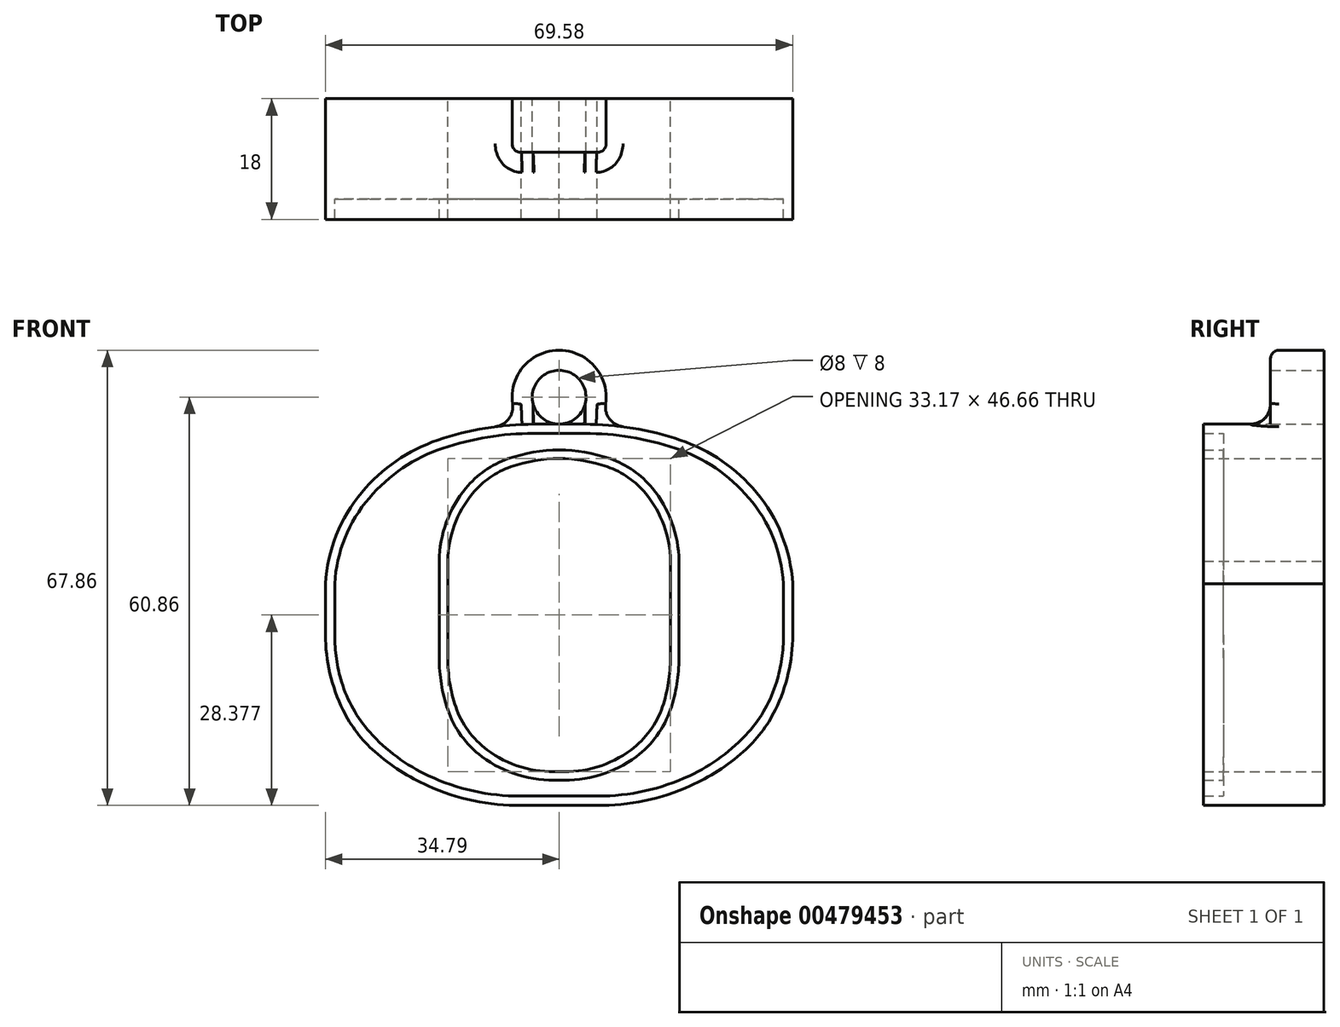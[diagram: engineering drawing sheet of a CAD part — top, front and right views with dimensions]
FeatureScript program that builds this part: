
annotation { "Feature Type Name" : "Feature", "Feature Type Description" : "" }
export const myFeature = defineFeature(function(context is Context, id is Id, definition is map)
    precondition{}
    {
        {
            var Q0;
            Q0=qCreatedBy(makeId("Front.planeOp"),FACE);
            var sketch = newSketch(context, id + "F0", { "sketchPlane" : qUnion([Q0])});
            skLineSegment(sketch, "E0", {"start": v(0, 23.85) * mm, "end": v(9.94, 23.85) * mm, "construction": true});
            skLineSegment(sketch, "E1", {"start": v(-16.59, 8.55) * mm, "end": v(-16.59, -5.87) * mm});
            skLineSegment(sketch, "E2", {"start": v(0, 23.85) * mm, "end": v(0, 28.97) * mm, "construction": true});
            skLineSegment(sketch, "E3", {"start": v(0, 28.97) * mm, "end": v(-3.73, 28.97) * mm});
            skArc(sketch, "E4", {"start": v(-3.73, 28.97) * mm, "mid": v(-11, 28.37) * mm, "end": v(-18.07, 26.6) * mm});
            skArc(sketch, "E5", {"start": v(-18.07, 26.6) * mm, "mid": v(-24.27, 23.48) * mm, "end": v(-29.4, 18.8) * mm});
            skArc(sketch, "E6", {"start": v(-29.4, 18.8) * mm, "mid": v(-33.17, 12.43) * mm, "end": v(-34.79, 5.2) * mm});
            skLineSegment(sketch, "E7", {"start": v(-34.79, 5.2) * mm, "end": v(-34.79, -2.41) * mm});
            skArc(sketch, "E8", {"start": v(-34.79, -2.41) * mm, "mid": v(-34.13, -8.18) * mm, "end": v(-32.18, -13.64) * mm});
            skArc(sketch, "E9", {"start": v(-32.18, -13.64) * mm, "mid": v(-30.11, -16.97) * mm, "end": v(-27.44, -19.84) * mm});
            skArc(sketch, "E10", {"start": v(-27.44, -19.84) * mm, "mid": v(-23.69, -22.68) * mm, "end": v(-19.55, -24.94) * mm});
            skArc(sketch, "E11", {"start": v(-19.55, -24.94) * mm, "mid": v(-12.76, -27.16) * mm, "end": v(-5.64, -27.86) * mm});
            skLineSegment(sketch, "E12", {"start": v(0, -22.8) * mm, "end": v(0, -27.86) * mm, "construction": true});
            skArc(sketch, "E13", {"start": v(0, 23.85) * mm, "mid": v(-3.64, 23.54) * mm, "end": v(-7.17, 22.63) * mm});
            skArc(sketch, "E14", {"start": v(-7.17, 22.63) * mm, "mid": v(-10.32, 21.01) * mm, "end": v(-12.9, 18.62) * mm});
            skArc(sketch, "E15", {"start": v(-12.9, 18.62) * mm, "mid": v(-15.6, 13.9) * mm, "end": v(-16.59, 8.55) * mm});
            skArc(sketch, "E16", {"start": v(-16.59, -5.87) * mm, "mid": v(-16.29, -9.56) * mm, "end": v(-15.4, -13.14) * mm});
            skArc(sketch, "E17", {"start": v(-15.4, -13.14) * mm, "mid": v(-13.55, -16.71) * mm, "end": v(-10.73, -19.57) * mm});
            skArc(sketch, "E18", {"start": v(-10.73, -19.57) * mm, "mid": v(-5.65, -22.13) * mm, "end": v(0, -22.8) * mm});
            skArc(sketch, "E19.0", {"start": v(-11.49, -20.59) * mm, "mid": v(-6.01, -23.35) * mm, "end": v(0.07, -24.06) * mm});
            skArc(sketch, "E19.1", {"start": v(-16.6, -13.55) * mm, "mid": v(-14.58, -17.46) * mm, "end": v(-11.49, -20.59) * mm});
            skArc(sketch, "E19.2", {"start": v(-17.86, -5.87) * mm, "mid": v(-17.54, -9.76) * mm, "end": v(-16.6, -13.55) * mm});
            skArc(sketch, "E19.3", {"start": v(0, 25.12) * mm, "mid": v(-3.85, 24.8) * mm, "end": v(-7.6, 23.82) * mm});
            skArc(sketch, "E19.4", {"start": v(-7.6, 23.82) * mm, "mid": v(-11.04, 22.06) * mm, "end": v(-13.89, 19.42) * mm});
            skArc(sketch, "E19.5", {"start": v(-13.89, 19.42) * mm, "mid": v(-16.8, 14.33) * mm, "end": v(-17.86, 8.56) * mm});
            skLineSegment(sketch, "E19.6", {"start": v(-17.86, 8.56) * mm, "end": v(-17.86, -5.87) * mm});
            skLineSegment(sketch, "E20", {"start": v(0, 27.6) * mm, "end": v(-3.8, 27.6) * mm});
            skArc(sketch, "E21", {"start": v(-3.8, 27.6) * mm, "mid": v(-10.65, 27.04) * mm, "end": v(-17.31, 25.39) * mm});
            skArc(sketch, "E22", {"start": v(-17.31, 25.39) * mm, "mid": v(-23.3, 22.43) * mm, "end": v(-28.27, 17.98) * mm});
            skArc(sketch, "E23", {"start": v(-28.27, 17.98) * mm, "mid": v(-31.9, 12) * mm, "end": v(-33.42, 5.2) * mm});
            skLineSegment(sketch, "E24", {"start": v(-33.42, 5.2) * mm, "end": v(-33.42, -2.42) * mm});
            skArc(sketch, "E25", {"start": v(-33.42, -2.42) * mm, "mid": v(-33.16, -6) * mm, "end": v(-32.38, -9.48) * mm});
            skArc(sketch, "E26", {"start": v(-32.38, -9.48) * mm, "mid": v(-30.7, -13.43) * mm, "end": v(-28.2, -16.93) * mm});
            skArc(sketch, "E27", {"start": v(-28.2, -16.93) * mm, "mid": v(-24.14, -20.63) * mm, "end": v(-19.43, -23.44) * mm});
            skArc(sketch, "E28", {"start": v(-19.43, -23.44) * mm, "mid": v(-12.77, -25.7) * mm, "end": v(-5.76, -26.45) * mm});
            skLineSegment(sketch, "E29", {"start": v(-5.76, -26.45) * mm, "end": v(0, -26.45) * mm});
            skArc(sketch, "E30.MirrorCS", {"start": v(34.79, -2.41) * mm, "mid": v(34.13, -8.18) * mm, "end": v(32.18, -13.64) * mm});
            skLineSegment(sketch, "E31.MirrorCS", {"start": v(34.79, 5.2) * mm, "end": v(34.79, -2.41) * mm});
            skArc(sketch, "E32.MirrorCS", {"start": v(29.4, 18.8) * mm, "mid": v(33.17, 12.43) * mm, "end": v(34.79, 5.2) * mm});
            skLineSegment(sketch, "E33.MirrorCS", {"start": v(0, 27.6) * mm, "end": v(3.8, 27.6) * mm});
            skLineSegment(sketch, "E34.MirrorCS", {"start": v(0, 28.97) * mm, "end": v(3.73, 28.97) * mm});
            skArc(sketch, "E35.MirrorCS", {"start": v(0, 25.12) * mm, "mid": v(3.85, 24.8) * mm, "end": v(7.6, 23.82) * mm});
            skArc(sketch, "E36.MirrorCS", {"start": v(0, 23.85) * mm, "mid": v(3.64, 23.54) * mm, "end": v(7.17, 22.63) * mm});
            skArc(sketch, "E37.MirrorCS", {"start": v(19.43, -23.44) * mm, "mid": v(12.77, -25.7) * mm, "end": v(5.76, -26.45) * mm});
            skLineSegment(sketch, "E38.MirrorCS", {"start": v(33.42, 5.2) * mm, "end": v(33.42, -2.42) * mm});
            skArc(sketch, "E39.MirrorCS", {"start": v(10.73, -19.57) * mm, "mid": v(5.65, -22.13) * mm, "end": v(0, -22.8) * mm});
            skArc(sketch, "E40.MirrorCS", {"start": v(12.9, 18.62) * mm, "mid": v(15.6, 13.9) * mm, "end": v(16.59, 8.55) * mm});
            skArc(sketch, "E41.MirrorCS", {"start": v(33.42, -2.42) * mm, "mid": v(33.16, -6) * mm, "end": v(32.38, -9.48) * mm});
            skArc(sketch, "E42.MirrorCS", {"start": v(13.89, 19.42) * mm, "mid": v(16.8, 14.33) * mm, "end": v(17.86, 8.56) * mm});
            skArc(sketch, "E43.MirrorCS", {"start": v(3.8, 27.6) * mm, "mid": v(10.65, 27.04) * mm, "end": v(17.31, 25.39) * mm});
            skArc(sketch, "E44.MirrorCS", {"start": v(27.44, -19.84) * mm, "mid": v(23.69, -22.68) * mm, "end": v(19.55, -24.94) * mm});
            skArc(sketch, "E45.MirrorCS", {"start": v(18.07, 26.6) * mm, "mid": v(24.27, 23.48) * mm, "end": v(29.4, 18.8) * mm});
            skArc(sketch, "E46.MirrorCS", {"start": v(28.2, -16.93) * mm, "mid": v(24.14, -20.63) * mm, "end": v(19.43, -23.44) * mm});
            skArc(sketch, "E47.MirrorCS", {"start": v(15.4, -13.14) * mm, "mid": v(13.55, -16.71) * mm, "end": v(10.73, -19.57) * mm});
            skArc(sketch, "E48.MirrorCS", {"start": v(11.49, -20.59) * mm, "mid": v(6.01, -23.35) * mm, "end": v(-0.07, -24.06) * mm});
            skArc(sketch, "E49.MirrorCS", {"start": v(28.27, 17.98) * mm, "mid": v(31.9, 12) * mm, "end": v(33.42, 5.2) * mm});
            skArc(sketch, "E50.MirrorCS", {"start": v(16.59, -5.87) * mm, "mid": v(16.29, -9.56) * mm, "end": v(15.4, -13.14) * mm});
            skArc(sketch, "E51.MirrorCS", {"start": v(7.6, 23.82) * mm, "mid": v(11.04, 22.06) * mm, "end": v(13.89, 19.42) * mm});
            skArc(sketch, "E52.MirrorCS", {"start": v(16.6, -13.55) * mm, "mid": v(14.58, -17.46) * mm, "end": v(11.49, -20.59) * mm});
            skArc(sketch, "E53.MirrorCS", {"start": v(3.73, 28.97) * mm, "mid": v(11, 28.37) * mm, "end": v(18.07, 26.6) * mm});
            skArc(sketch, "E54.MirrorCS", {"start": v(17.31, 25.39) * mm, "mid": v(23.3, 22.43) * mm, "end": v(28.27, 17.98) * mm});
            skArc(sketch, "E55.MirrorCS", {"start": v(7.17, 22.63) * mm, "mid": v(10.32, 21.01) * mm, "end": v(12.9, 18.62) * mm});
            skLineSegment(sketch, "E56.MirrorCS", {"start": v(16.59, 8.55) * mm, "end": v(16.59, -5.87) * mm});
            skArc(sketch, "E57.MirrorCS", {"start": v(32.18, -13.64) * mm, "mid": v(30.11, -16.97) * mm, "end": v(27.44, -19.84) * mm});
            skArc(sketch, "E58.MirrorCS", {"start": v(17.86, -5.87) * mm, "mid": v(17.54, -9.76) * mm, "end": v(16.6, -13.55) * mm});
            skLineSegment(sketch, "E59.MirrorCS", {"start": v(5.76, -26.45) * mm, "end": v(0, -26.45) * mm});
            skLineSegment(sketch, "E60.MirrorCS", {"start": v(17.86, 8.56) * mm, "end": v(17.86, -5.87) * mm});
            skArc(sketch, "E61.MirrorCS", {"start": v(19.55, -24.94) * mm, "mid": v(12.76, -27.16) * mm, "end": v(5.64, -27.86) * mm});
            skArc(sketch, "E62.MirrorCS", {"start": v(32.38, -9.48) * mm, "mid": v(30.7, -13.43) * mm, "end": v(28.2, -16.93) * mm});
            skLineSegment(sketch, "E63", {"start": v(-5.64, -27.86) * mm, "end": v(5.64, -27.86) * mm});
            skSolve(sketch);
        }
        {
            var Q0;
            Q0 = qSketchRegion(id + "F0", true);
            var Q1;
            Q1=makeQuery(id+"F0.imprint","IMPRINT",FACE,{"disambiguationData":[TD([[makeQuery(id+"F0.imprint","IMPRINT",EDGE,{"derivedFrom":sQuery(id+"F0.wireOp",EDGE,"E1")}),-1.0]])]});
            var Q2;
            {var subQ0=sQuery(id+"F0.wireOp",EDGE,"E19.1");Q2=makeQuery(id+"F0.imprint","IMPRINT",FACE,{"disambiguationData":[TD([[makeQuery(id+"F0.imprint","IMPRINT",EDGE,{"derivedFrom":subQ0}),-1.0]])]});}
            extrude(context, id + "F1", {"entities" : qUnion([Q0, Q1, Q2]), "depth" : 15 * mm});
        }
        {
            var Q0;
            Q0=makeQuery(id+"F0.imprint","IMPRINT",FACE,{"disambiguationData":[TD([[makeQuery(id+"F0.imprint","IMPRINT",EDGE,{"derivedFrom":sQuery(id+"F0.wireOp",EDGE,"E1")}),-1.0]])]});
            var Q1;
            Q1=makeQuery(id+"F0.imprint","IMPRINT",FACE,{"disambiguationData":[TD([[makeQuery(id+"F0.imprint","IMPRINT",EDGE,{"derivedFrom":sQuery(id+"F0.wireOp",EDGE,"E3")}),1.0]])]});
            extrude(context, id + "F2", {"entities" : qUnion([Q0, Q1]), "operationType" : NewBodyOperationType.ADD, "depth" : 18 * mm});
        }
        {
            var Q0;
            Q0=qCreatedBy(makeId("Front.planeOp"),FACE);
            var sketch = newSketch(context, id + "F3", { "sketchPlane" : qUnion([Q0])});
            skLineSegment(sketch, "E64", {"start": v(0, 0) * mm, "end": v(0, 26) * mm});
            skCircle(sketch, "E65", {"center": v(0, 33) * mm, "radius": 7 * mm});
            skCircle(sketch, "E66", {"center": v(0, 33) * mm, "radius": 4 * mm});
            skSolve(sketch);
        }
        {
            var Q0;
            Q0 = qSketchRegion(id + "F3", true);
            extrude(context, id + "F4", {"entities" : qUnion([Q0]), "operationType" : NewBodyOperationType.ADD, "depth" : 8 * mm});
        }
        {
            var Q0;
            Q0=makeQuery(id+"F4.opExtrude","CAP_EDGE",EDGE,{"disambiguationData":[OSD([sQuery(id+"F3.wireOp",EDGE,"E65")])],"isStart":false});
            fillet(context, id + "F5", {"entities" : qUnion([Q0]), "radius" : 1.25 * mm, "tangentPropagation" : true, "allowEdgeOverflow" : false});
        }
        {
            var Q0;
            {var subQ0=sQuery(id+"F0.wireOp",EDGE,"E53.MirrorCS");Q0=makeQuery(id+"F4.boolean.opBoolean","INTERSECT",EDGE,{"derivedFrom":[makeQuery(id+"F2.boolean.opBoolean","MERGE",FACE,{"derivedFrom":[makeQuery(id+"F1.opExtrude","SWEPT_FACE",FACE,{"disambiguationData":[OSD([subQ0])]}),makeQuery(id+"F2.opExtrude","SWEPT_FACE",FACE,{"disambiguationData":[OSD([subQ0])]})]}),makeQuery(id+"F4.opExtrude","SWEPT_FACE",FACE,{"disambiguationData":[OSD([sQuery(id+"F3.wireOp",EDGE,"E65")])]})]});}
            var Q1;
            {var subQ0=sQuery(id+"F0.wireOp",EDGE,"E4");Q1=makeQuery(id+"F4.boolean.opBoolean","INTERSECT",EDGE,{"derivedFrom":[makeQuery(id+"F2.boolean.opBoolean","MERGE",FACE,{"derivedFrom":[makeQuery(id+"F1.opExtrude","SWEPT_FACE",FACE,{"disambiguationData":[OSD([subQ0])]}),makeQuery(id+"F2.opExtrude","SWEPT_FACE",FACE,{"disambiguationData":[OSD([subQ0])]})]}),makeQuery(id+"F4.opExtrude","SWEPT_FACE",FACE,{"disambiguationData":[OSD([sQuery(id+"F3.wireOp",EDGE,"E65")])]})]});}
            fillet(context, id + "F6", {"entities" : qUnion([Q0, Q1]), "radius" : 3 * mm, "tangentPropagation" : true, "allowEdgeOverflow" : false});
        }
    });
